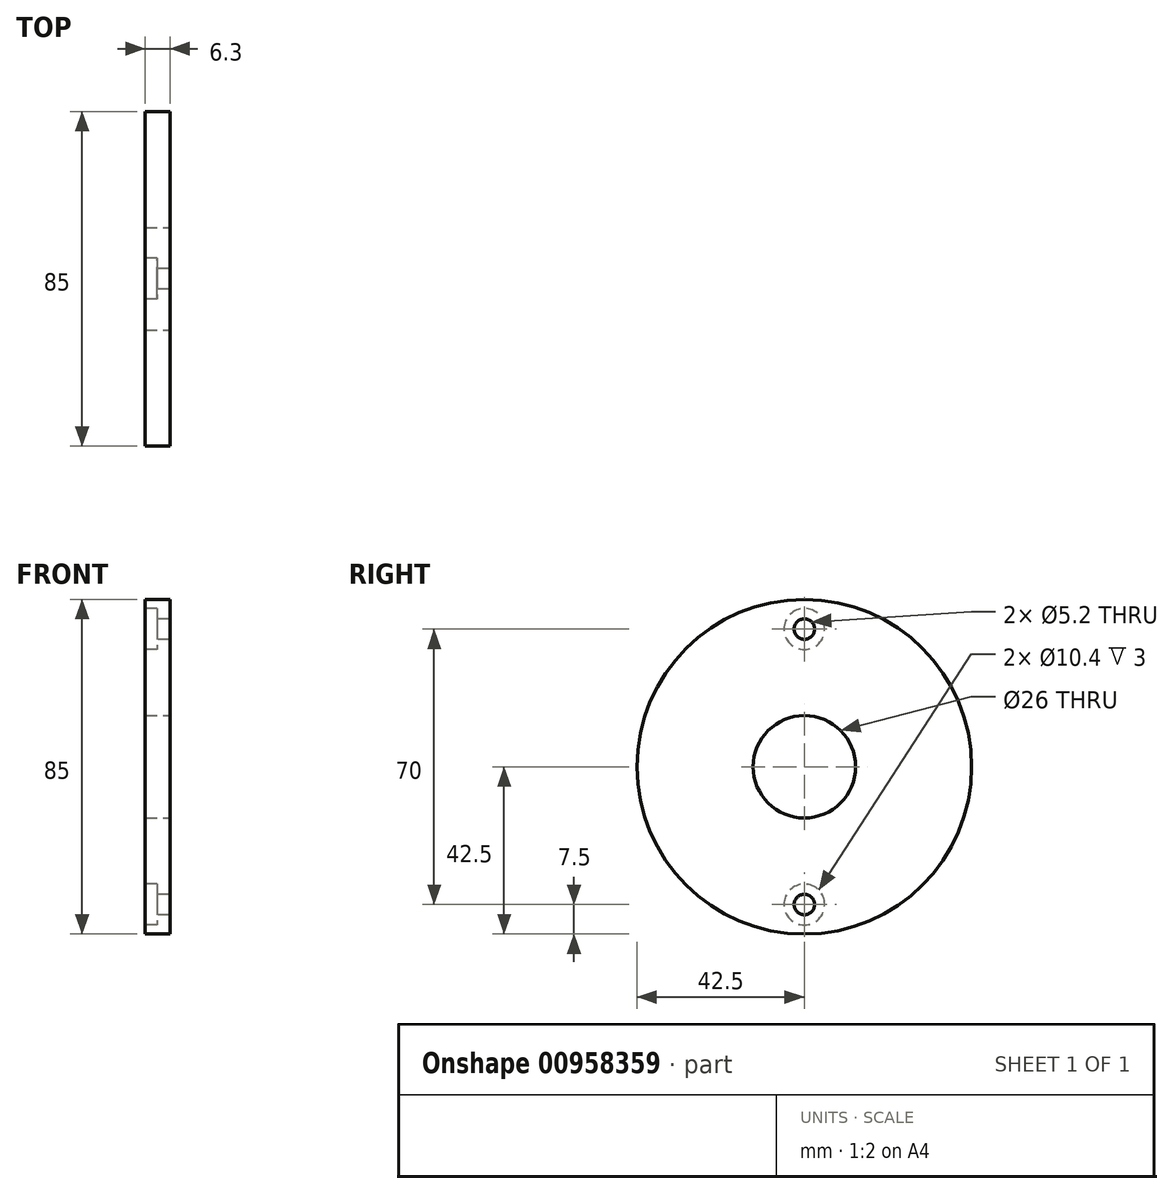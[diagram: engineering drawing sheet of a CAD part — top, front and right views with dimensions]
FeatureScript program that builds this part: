
annotation { "Feature Type Name" : "Feature", "Feature Type Description" : "" }
export const myFeature = defineFeature(function(context is Context, id is Id, definition is map)
    precondition{}
    {
        {
            var Q0;
            Q0=qCreatedBy(makeId("Front.planeOp"),FACE);
            var sketch = newSketch(context, id + "F0", { "sketchPlane" : qUnion([Q0])});
            skLineSegment(sketch, "E0.bottom", {"start": v(8.75, 42.5) * mm, "end": v(2.45, 42.5) * mm});
            skLineSegment(sketch, "E0.top", {"start": v(8.75, 13) * mm, "end": v(2.45, 13) * mm});
            skLineSegment(sketch, "E0.left", {"start": v(8.75, 42.5) * mm, "end": v(8.75, 13) * mm});
            skLineSegment(sketch, "E0.right", {"start": v(2.45, 42.5) * mm, "end": v(2.45, 13) * mm});
            skLineSegment(sketch, "E1", {"start": v(0, 0) * mm, "end": v(-9.37, 0) * mm});
            skSolve(sketch);
        }
        {
            var Q0;
            Q0=qSketchRegion(id+"F0",true);
            var Q1;
            Q1=sQuery(id+"F0.wireOp",EDGE,"E1");
            revolve(context, id + "F1", {"surfaceOperationType" : NewSurfaceOperationType.NEW, "entities" : qUnion([Q0]), "axis" : qUnion([Q1]), "revolveType" : RevolveType.FULL});
        }
        {
            var Q0;
            Q0=makeQuery(id+"F1.opRevolve","SWEPT_FACE",FACE,{"disambiguationData":[OSD([sQuery(id+"F0.wireOp",EDGE,"E0.right")])]});
            var sketch = newSketch(context, id + "F2", { "sketchPlane" : qUnion([Q0])});
            skCircle(sketch, "E2", {"center": v(0, 35) * mm, "radius": 2.6 * mm});
            skCircle(sketch, "E3", {"center": v(0, -35) * mm, "radius": 2.6 * mm});
            skSolve(sketch);
        }
        {
            var Q0;
            Q0 = qSketchRegion(id + "F2", true);
            extrude(context, id + "F3", {"entities" : qUnion([Q0]), "operationType" : NewBodyOperationType.REMOVE, "oppositeDirection" : true, "depth" : 25 * mm, "offsetDistance" : 25 * mm});
        }
        {
            var Q0;
            Q0=makeQuery(id+"F1.opRevolve","SWEPT_FACE",FACE,{"disambiguationData":[OSD([sQuery(id+"F0.wireOp",EDGE,"E0.right")])]});
            var sketch = newSketch(context, id + "F4", { "sketchPlane" : qUnion([Q0])});
            skCircle(sketch, "E4", {"center": v(0, 35) * mm, "radius": 5.2 * mm});
            skCircle(sketch, "E5", {"center": v(0, -35) * mm, "radius": 5.2 * mm});
            skSolve(sketch);
        }
        {
            var Q0;
            Q0=makeQuery(id+"F4.imprint","IMPRINT",FACE,{"disambiguationData":[TD([[makeQuery(id+"F4.imprint","IMPRINT",EDGE,{"derivedFrom":sQuery(id+"F4.wireOp",EDGE,"E4")}),1.0]])]});
            var Q1;
            Q1=makeQuery(id+"F4.imprint","IMPRINT",FACE,{"disambiguationData":[TD([[makeQuery(id+"F4.imprint","IMPRINT",EDGE,{"derivedFrom":sQuery(id+"F4.wireOp",EDGE,"E5")}),1.0]])]});
            extrude(context, id + "F5", {"entities" : qUnion([Q0, Q1]), "operationType" : NewBodyOperationType.REMOVE, "oppositeDirection" : true, "depth" : 3 * mm, "offsetDistance" : 25 * mm});
        }
    });
